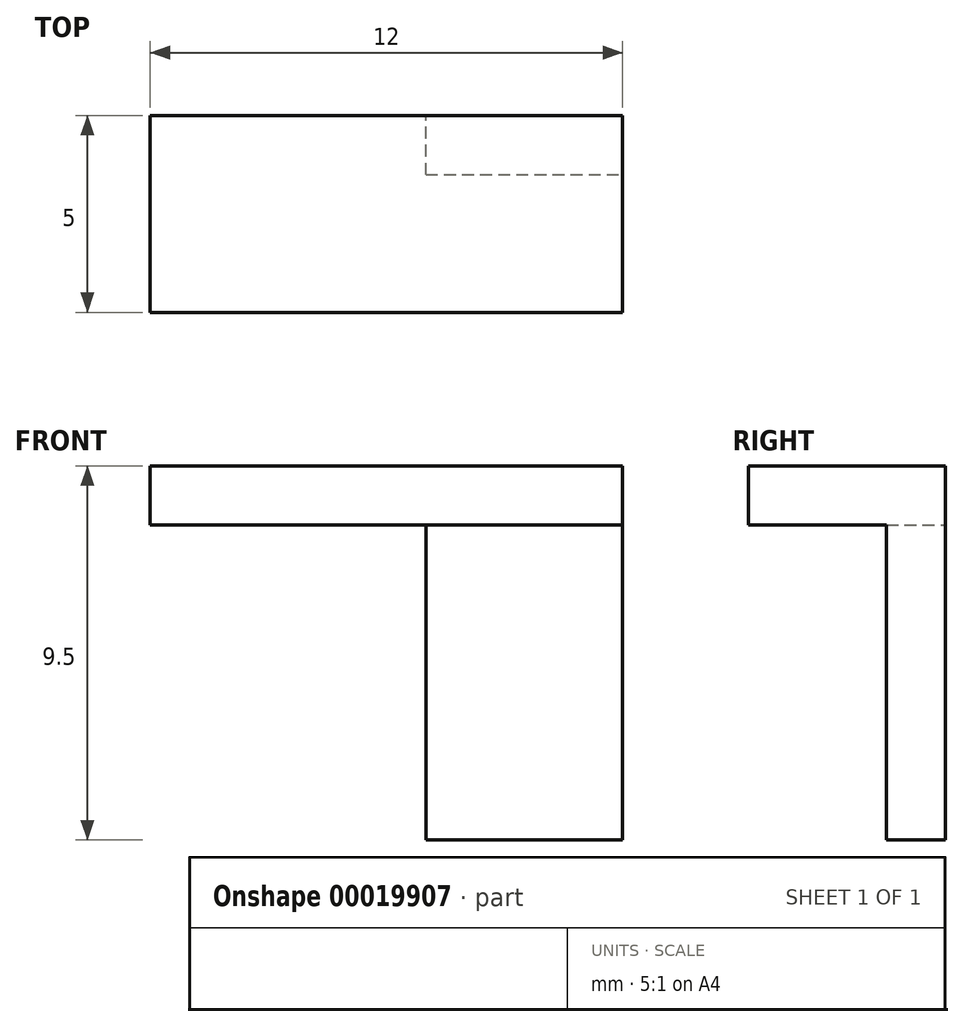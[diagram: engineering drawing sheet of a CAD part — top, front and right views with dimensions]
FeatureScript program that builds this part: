
annotation { "Feature Type Name" : "Feature", "Feature Type Description" : "" }
export const myFeature = defineFeature(function(context is Context, id is Id, definition is map)
    precondition{}
    {
        {
            var Q0;
            Q0=qCreatedBy(makeId("Top.planeOp"),FACE);
            var sketch = newSketch(context, id + "F0", { "sketchPlane" : qUnion([Q0])});
            skLineSegment(sketch, "E0.bottom", {"start": v(0, 0) * mm, "end": v(12, 0) * mm});
            skLineSegment(sketch, "E0.top", {"start": v(0, 5) * mm, "end": v(12, 5) * mm});
            skLineSegment(sketch, "E0.left", {"start": v(0, 0) * mm, "end": v(0, 5) * mm});
            skLineSegment(sketch, "E0.right", {"start": v(12, 0) * mm, "end": v(12, 5) * mm});
            skSolve(sketch);
        }
        {
            var Q0;
            Q0 = qSketchRegion(id + "F0", true);
            extrude(context, id + "F1", {"entities" : qUnion([Q0]), "depth" : 1.5 * mm});
        }
        {
            var Q0;
            Q0=makeQuery(id+"F1.opExtrude","CAP_FACE",FACE,{"disambiguationData":[OSD([sQuery(id+"F0.wireOp",EDGE,"E0.bottom"),sQuery(id+"F0.wireOp",EDGE,"E0.top"),sQuery(id+"F0.wireOp",EDGE,"E0.left"),sQuery(id+"F0.wireOp",EDGE,"E0.right")])],"isStart":true});
            var sketch = newSketch(context, id + "F2", { "sketchPlane" : qUnion([Q0])});
            skLineSegment(sketch, "E1.bottom", {"start": v(7, -5) * mm, "end": v(12, -5) * mm});
            skLineSegment(sketch, "E1.top", {"start": v(7, -3.5) * mm, "end": v(12, -3.5) * mm});
            skLineSegment(sketch, "E1.left", {"start": v(7, -3.5) * mm, "end": v(7, -5) * mm});
            skLineSegment(sketch, "E1.right", {"start": v(12, -3.5) * mm, "end": v(12, -5) * mm});
            skSolve(sketch);
        }
        {
            var Q0;
            Q0 = qSketchRegion(id + "F2", true);
            extrude(context, id + "F3", {"entities" : qUnion([Q0]), "operationType" : NewBodyOperationType.ADD, "depth" : 8 * mm});
        }
    });
